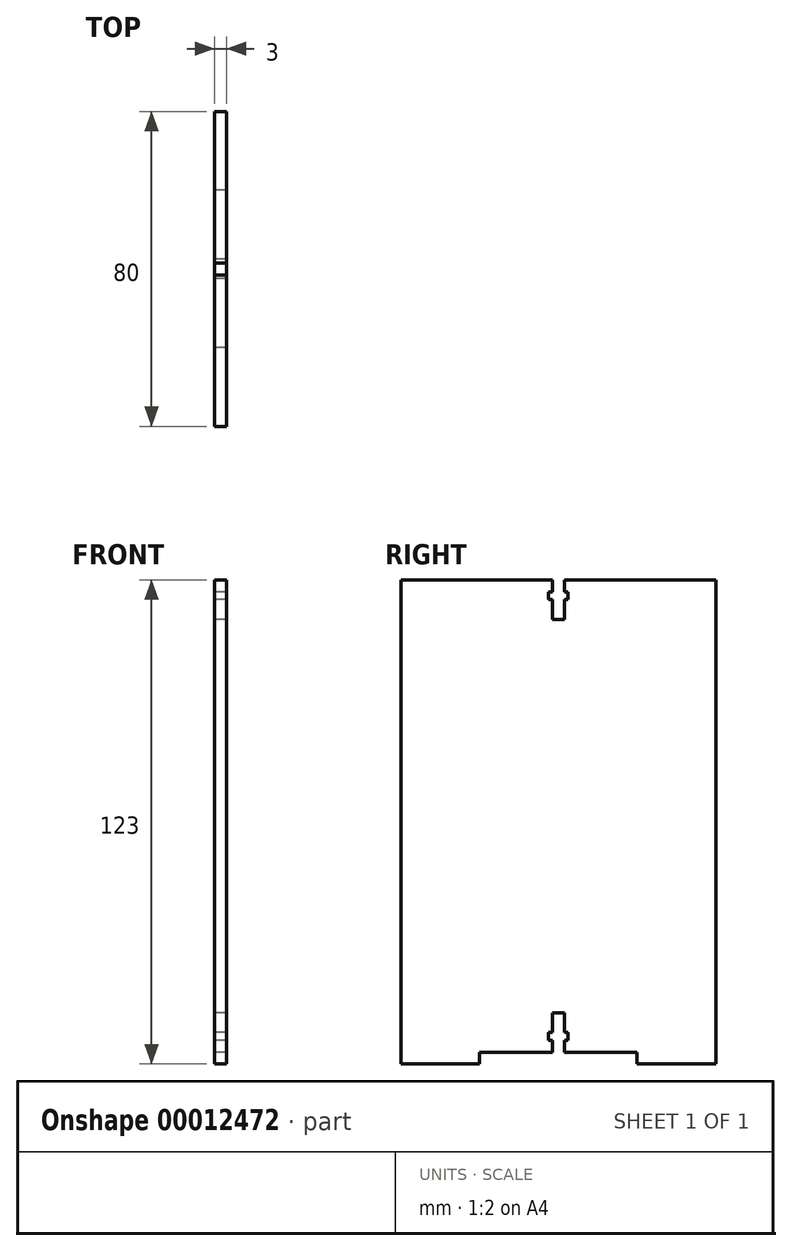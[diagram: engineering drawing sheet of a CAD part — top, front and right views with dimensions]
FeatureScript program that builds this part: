
annotation { "Feature Type Name" : "Feature", "Feature Type Description" : "" }
export const myFeature = defineFeature(function(context is Context, id is Id, definition is map)
    precondition{}
    {
        {
            var Q0;
            Q0=qCreatedBy(makeId("Right.planeOp"),FACE);
            var sketch = newSketch(context, id + "F0", { "sketchPlane" : qUnion([Q0])});
            skLineSegment(sketch, "E0.bottom", {"start": v(-40, 70.42) * mm, "end": v(40, 70.42) * mm});
            skLineSegment(sketch, "E0.top", {"start": v(-40, -49.58) * mm, "end": v(40, -49.58) * mm});
            skLineSegment(sketch, "E0.left", {"start": v(-40, 70.42) * mm, "end": v(-40, -49.58) * mm});
            skLineSegment(sketch, "E0.right", {"start": v(40, 70.42) * mm, "end": v(40, -49.58) * mm});
            skLineSegment(sketch, "E1.bottom", {"start": v(-40, 70.42) * mm, "end": v(-20, 70.42) * mm});
            skLineSegment(sketch, "E1.top", {"start": v(-40, 73.42) * mm, "end": v(-20, 73.42) * mm});
            skLineSegment(sketch, "E1.left", {"start": v(-40, 70.42) * mm, "end": v(-40, 73.42) * mm});
            skLineSegment(sketch, "E1.right", {"start": v(-20, 70.42) * mm, "end": v(-20, 73.42) * mm});
            skLineSegment(sketch, "E2.bottom", {"start": v(40, 70.42) * mm, "end": v(20, 70.42) * mm});
            skLineSegment(sketch, "E2.top", {"start": v(40, 73.42) * mm, "end": v(20, 73.42) * mm});
            skLineSegment(sketch, "E2.left", {"start": v(40, 70.42) * mm, "end": v(40, 73.42) * mm});
            skLineSegment(sketch, "E2.right", {"start": v(20, 70.42) * mm, "end": v(20, 73.42) * mm});
            skLineSegment(sketch, "E3.bottom", {"start": v(-40, -49.58) * mm, "end": v(-20, -49.58) * mm});
            skLineSegment(sketch, "E3.top", {"start": v(-40, -52.58) * mm, "end": v(-20, -52.58) * mm});
            skLineSegment(sketch, "E3.left", {"start": v(-40, -49.58) * mm, "end": v(-40, -52.58) * mm});
            skLineSegment(sketch, "E3.right", {"start": v(-20, -49.58) * mm, "end": v(-20, -52.58) * mm});
            skLineSegment(sketch, "E4.bottom", {"start": v(40, -49.58) * mm, "end": v(20, -49.58) * mm});
            skLineSegment(sketch, "E4.top", {"start": v(40, -52.58) * mm, "end": v(20, -52.58) * mm});
            skLineSegment(sketch, "E4.left", {"start": v(40, -49.58) * mm, "end": v(40, -52.58) * mm});
            skLineSegment(sketch, "E4.right", {"start": v(20, -49.58) * mm, "end": v(20, -52.58) * mm});
            skLineSegment(sketch, "E5", {"start": v(-40, 10.42) * mm, "end": v(40, 10.42) * mm, "construction": true});
            skLineSegment(sketch, "E6", {"start": v(0, 70.42) * mm, "end": v(0, -49.58) * mm, "construction": true});
            skLineSegment(sketch, "E7", {"start": v(1.5, 70.42) * mm, "end": v(1.5, 67.42) * mm});
            skLineSegment(sketch, "E8", {"start": v(1.5, 67.42) * mm, "end": v(2.5, 67.42) * mm});
            skLineSegment(sketch, "E9", {"start": v(2.5, 67.42) * mm, "end": v(2.5, 65.42) * mm});
            skLineSegment(sketch, "E10", {"start": v(2.5, 65.42) * mm, "end": v(1.5, 65.42) * mm});
            skLineSegment(sketch, "E11", {"start": v(1.5, 65.42) * mm, "end": v(1.5, 60.42) * mm});
            skLineSegment(sketch, "E12", {"start": v(1.5, 60.42) * mm, "end": v(-1.5, 60.42) * mm});
            skLineSegment(sketch, "E13", {"start": v(-1.5, 60.42) * mm, "end": v(-1.5, 65.42) * mm});
            skLineSegment(sketch, "E14", {"start": v(-1.5, 65.42) * mm, "end": v(-2.5, 65.42) * mm});
            skLineSegment(sketch, "E15", {"start": v(-2.5, 65.42) * mm, "end": v(-2.5, 67.42) * mm});
            skLineSegment(sketch, "E16", {"start": v(-2.5, 67.42) * mm, "end": v(-1.5, 67.42) * mm});
            skLineSegment(sketch, "E17", {"start": v(-1.5, 67.42) * mm, "end": v(-1.5, 70.42) * mm});
            skLineSegment(sketch, "E18.0.MirrorCS", {"start": v(-1.5, -44.58) * mm, "end": v(-2.5, -44.58) * mm});
            skLineSegment(sketch, "E18.1.MirrorCS", {"start": v(-2.5, -44.58) * mm, "end": v(-2.5, -46.58) * mm});
            skLineSegment(sketch, "E18.2.MirrorCS", {"start": v(-2.5, -46.58) * mm, "end": v(-1.5, -46.58) * mm});
            skLineSegment(sketch, "E18.3.MirrorCS", {"start": v(-1.5, -46.58) * mm, "end": v(-1.5, -49.58) * mm});
            skLineSegment(sketch, "E18.4.MirrorCS", {"start": v(1.5, -49.58) * mm, "end": v(1.5, -46.58) * mm});
            skLineSegment(sketch, "E18.5.MirrorCS", {"start": v(1.5, -46.58) * mm, "end": v(2.5, -46.58) * mm});
            skLineSegment(sketch, "E18.6.MirrorCS", {"start": v(2.5, -46.58) * mm, "end": v(2.5, -44.58) * mm});
            skLineSegment(sketch, "E18.7.MirrorCS", {"start": v(2.5, -44.58) * mm, "end": v(1.5, -44.58) * mm});
            skLineSegment(sketch, "E18.8.MirrorCS", {"start": v(1.5, -44.58) * mm, "end": v(1.5, -39.58) * mm});
            skLineSegment(sketch, "E18.9.MirrorCS", {"start": v(1.5, -39.58) * mm, "end": v(-1.5, -39.58) * mm});
            skLineSegment(sketch, "E18.10.MirrorCS", {"start": v(-1.5, -39.58) * mm, "end": v(-1.5, -44.58) * mm});
            skSolve(sketch);
        }
        {
            var Q0;
            {var subQ9=sQuery(id+"F0.wireOp",EDGE,"E0.left");Q0=makeQuery(id+"F0.imprint","IMPRINT",FACE,{"disambiguationData":[TD([[makeQuery(id+"F0.imprint","IMPRINT",EDGE,{"derivedFrom":subQ9}),1.0]])]});}
            var Q1;
            Q1=makeQuery(id+"F0.imprint","IMPRINT",FACE,{"disambiguationData":[TD([[makeQuery(id+"F0.imprint","IMPRINT",EDGE,{"derivedFrom":sQuery(id+"F0.wireOp",EDGE,"E4.right")}),1.0]])]});
            var Q2;
            {var subQ1=sQuery(id+"F0.wireOp",EDGE,"E3.right");Q2=makeQuery(id+"F0.imprint","IMPRINT",FACE,{"disambiguationData":[TD([[makeQuery(id+"F0.imprint","IMPRINT",EDGE,{"derivedFrom":subQ1}),-1.0]])]});}
            var Q3;
            Q3=makeQuery(id+"F0.imprint","IMPRINT",FACE,{"disambiguationData":[TD([[makeQuery(id+"F0.imprint","IMPRINT",EDGE,{"derivedFrom":sQuery(id+"F0.wireOp",EDGE,"E1.bottom")}),1.0]])]});
            var Q4;
            Q4=makeQuery(id+"F0.imprint","IMPRINT",FACE,{"disambiguationData":[TD([[makeQuery(id+"F0.imprint","IMPRINT",EDGE,{"derivedFrom":sQuery(id+"F0.wireOp",EDGE,"E2.bottom")}),-1.0]])]});
            extrude(context, id + "F1", {"entities" : qUnion([Q0, Q1, Q2, Q3, Q4]), "depth" : 3 * mm});
        }
    });
